# Revit family: T200028
name_source: partatom
category: Furniture
revit_build: Autodesk Revit Architecture 2013 (Build: 20120221_2030(x64)
units: mm (PartAtom-declared; Revit-internal decimal feet)

## types (1)
- T200028
    Assembly Code = E2020200
    Back Coverage Material = OFS BRANDS INTERMIX WORK Back Coverage Plastic
    Catalog = http://ofsbrands.com
    Chassis Material = OFS BRANDS INTERMIX WORK Chassis Wood
    Conector Clip Material = OFS BRANDS INTERMIX WORK Conector Clip Metal
    Conector Material = OFS BRANDS INTERMIX WORK Conector Metal
    Cushion Material = OFS BRANDS INTERMIX WORK Cushion Fabric
    Depth = 332 5/16"
    Description = OFS BRANDS FIRST OFFICE INTERMIX WORK TYPICAL T200028
    Drawer Front Material = OFS BRANDS INTERMIX WORK Drawer Front Wood
    Feet Material = OFS BRANDS INTERMIX WORK Feet Metal
    Glides Material = OFS BRANDS INTERMIX WORK Glide Plastic
    Grommet  Material = OFS BRANDS INTERMIX WORK Grommet Metal
    Height = 42"
    Lock Material = OFS BRANDS INTERMIX WORK Lock Metal
    Manufacturer = FIRST OFFICE
    Model = T200028
    Pull Material = OFS BRANDS INTERMIX WORK Pull Metal
    Roll Material = OFS BRANDS INTERMIX WORK Roll Plastic
    Tackboard Material = OFS BRANDS INTERMIX WORK Tackboard Fabric
    Tool Rail Material = OFS BRANDS INTERMIX WORK Tool Rail Metal
    Top Core Material = OFS BRANDS INTERMIX WORK Top Core Wood
    URL = http://www.ofsbrands.com
    Width = 312 3/16"

## geometry (parser evidence)
native form markers: Blend x19, Sweep x2
no freeform markers — native parametric forms only
